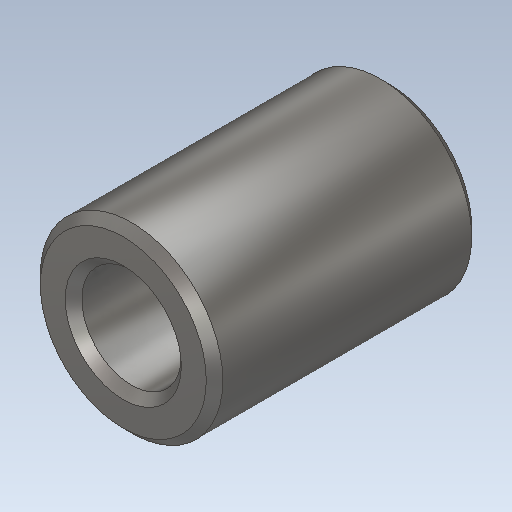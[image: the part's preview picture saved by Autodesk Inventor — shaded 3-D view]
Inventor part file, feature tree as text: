
AUTODESK INVENTOR PART (.ipt)
format: ipt  version: 2020 (Build 240168000, 168)  size: 146,944 bytes
history: native  units: mm
features: other x1, extrude x1, chamfer x1, sketch x1
ambient origin geometry x8: Origin, YZ Plane, XZ Plane, XY Plane, X Axis, Y Axis, Z Axis, Center Point
bodies: Body1 (feature_tree)
feature tree (4):
  other  "Bryła1"
  extrude  "Wyciągnięcie proste1"  Depth=12.0mm
  chamfer  "Faza1"  Distance=22.0mm
  sketch  "Szkic1"
